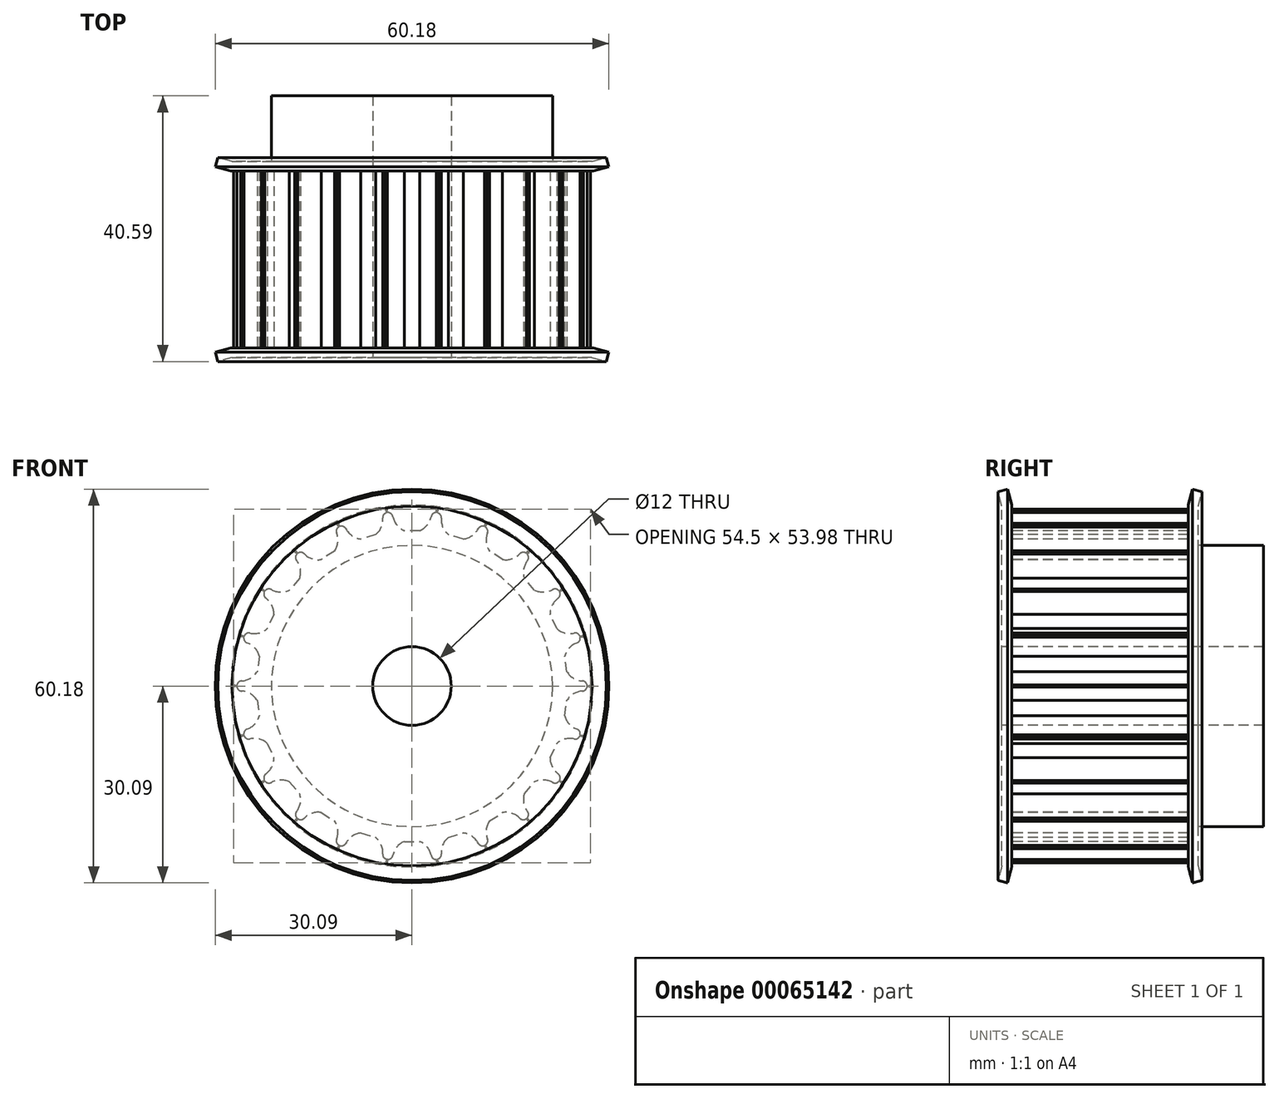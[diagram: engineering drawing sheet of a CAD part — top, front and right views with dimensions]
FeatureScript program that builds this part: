
annotation { "Feature Type Name" : "Feature", "Feature Type Description" : "" }
export const myFeature = defineFeature(function(context is Context, id is Id, definition is map)
    precondition{}
    {
        {
            var Q0;
            Q0=qCreatedBy(makeId("Right.planeOp"),FACE);
            var sketch = newSketch(context, id + "F0", { "sketchPlane" : qUnion([Q0])});
            skLineSegment(sketch, "E0", {"start": v(-21.52, 0) * mm, "end": v(23.89, 0) * mm, "construction": true});
            skLineSegment(sketch, "E1", {"start": v(0, 6) * mm, "end": v(0, 27.25) * mm});
            skLineSegment(sketch, "E2", {"start": v(0, 27.25) * mm, "end": v(30, 27.25) * mm});
            skLineSegment(sketch, "E3", {"start": v(30, 27.25) * mm, "end": v(30, 21.5) * mm});
            skLineSegment(sketch, "E4", {"start": v(30, 21.5) * mm, "end": v(40, 21.5) * mm});
            skLineSegment(sketch, "E5", {"start": v(40, 21.5) * mm, "end": v(40, 6) * mm});
            skLineSegment(sketch, "E6", {"start": v(40, 6) * mm, "end": v(0, 6) * mm});
            skSolve(sketch);
        }
        {
            var Q0;
            Q0 = qSketchRegion(id + "F0", true);
            var Q1;
            Q1=sQuery(id+"F0.wireOp",EDGE,"E0");
            revolve(context, id + "F1", {"entities" : qUnion([Q0]), "axis" : qUnion([Q1]), "revolveType" : RevolveType.FULL});
        }
        {
            var Q0;
            Q0=makeQuery(id+"F1.opRevolve","SWEPT_FACE",FACE,{"disambiguationData":[OSD([sQuery(id+"F0.wireOp",EDGE,"E1")])]});
            var sketch = newSketch(context, id + "F2", { "sketchPlane" : qUnion([Q0])});
            skArc(sketch, "E7", {"start": v(-2.94, 25.9) * mm, "mid": v(-2.33, 24.61) * mm, "end": v(-1.2, 23.75) * mm});
            skLineSegment(sketch, "E8.bottom", {"start": v(-3.75, 28.5) * mm, "end": v(3.75, 28.5) * mm});
            skLineSegment(sketch, "E8.top", {"start": v(-3.75, 26.5) * mm, "end": v(-3.67, 26.5) * mm});
            skLineSegment(sketch, "E8.left", {"start": v(-3.75, 28.5) * mm, "end": v(-3.75, 26.5) * mm});
            skLineSegment(sketch, "E8.right", {"start": v(3.75, 28.5) * mm, "end": v(3.75, 26.5) * mm});
            skArc(sketch, "E9.filletArc", {"start": v(-2.94, 25.9) * mm, "mid": v(-3.2, 26.33) * mm, "end": v(-3.67, 26.5) * mm});
            skLineSegment(sketch, "E10", {"start": v(3.67, 26.5) * mm, "end": v(3.75, 26.5) * mm});
            skPoint(sketch, "E11.visualSharp", {"position": v(3, 26.5) * mm});
            skArc(sketch, "E11.filletArc", {"start": v(3.67, 26.5) * mm, "mid": v(3.2, 26.33) * mm, "end": v(2.94, 25.9) * mm});
            skLineSegment(sketch, "E12", {"start": v(-1.2, 23.75) * mm, "end": v(1.2, 23.75) * mm});
            skArc(sketch, "E13.trimOffspring", {"start": v(1.2, 23.75) * mm, "mid": v(2.33, 24.61) * mm, "end": v(2.94, 25.9) * mm});
            skLineSegment(sketch, "E14.1.0", {"start": v(-11.63, 26.29) * mm, "end": v(-4.43, 28.4) * mm});
            skLineSegment(sketch, "E14.1.1", {"start": v(-11.63, 26.29) * mm, "end": v(-11.06, 24.37) * mm});
            skArc(sketch, "E14.1.2", {"start": v(-10.12, 24.02) * mm, "mid": v(-10.49, 24.36) * mm, "end": v(-11, 24.4) * mm});
            skArc(sketch, "E14.1.3", {"start": v(-10.12, 24.02) * mm, "mid": v(-9.17, 22.96) * mm, "end": v(-7.84, 22.45) * mm});
            skLineSegment(sketch, "E14.1.4", {"start": v(-7.84, 22.45) * mm, "end": v(-5.54, 23.13) * mm});
            skArc(sketch, "E14.1.5", {"start": v(-5.54, 23.13) * mm, "mid": v(-4.7, 24.27) * mm, "end": v(-4.48, 25.68) * mm});
            skPoint(sketch, "E14.1.6", {"position": v(-4.59, 26.27) * mm});
            skLineSegment(sketch, "E14.1.7", {"start": v(-4.43, 28.4) * mm, "end": v(-3.87, 26.48) * mm});
            skArc(sketch, "E14.1.8", {"start": v(-3.94, 26.46) * mm, "mid": v(-4.35, 26.17) * mm, "end": v(-4.48, 25.68) * mm});
            skLineSegment(sketch, "E14.2.0", {"start": v(-18.56, 21.95) * mm, "end": v(-12.25, 26) * mm});
            skLineSegment(sketch, "E14.2.1", {"start": v(-18.56, 21.95) * mm, "end": v(-17.48, 20.27) * mm});
            skArc(sketch, "E14.2.2", {"start": v(-16.48, 20.2) * mm, "mid": v(-16.93, 20.42) * mm, "end": v(-17.42, 20.3) * mm});
            skArc(sketch, "E14.2.3", {"start": v(-16.48, 20.2) * mm, "mid": v(-15.27, 19.44) * mm, "end": v(-13.85, 19.33) * mm});
            skLineSegment(sketch, "E14.2.4", {"start": v(-13.85, 19.33) * mm, "end": v(-11.83, 20.63) * mm});
            skArc(sketch, "E14.2.5", {"start": v(-11.83, 20.63) * mm, "mid": v(-11.34, 21.97) * mm, "end": v(-11.53, 23.38) * mm});
            skPoint(sketch, "E14.2.6", {"position": v(-11.8, 23.92) * mm});
            skLineSegment(sketch, "E14.2.7", {"start": v(-12.25, 26) * mm, "end": v(-11.17, 24.32) * mm});
            skArc(sketch, "E14.2.8", {"start": v(-11.24, 24.28) * mm, "mid": v(-11.54, 23.88) * mm, "end": v(-11.53, 23.38) * mm});
            skLineSegment(sketch, "E14.3.0", {"start": v(-24, 15.83) * mm, "end": v(-19.08, 21.5) * mm});
            skLineSegment(sketch, "E14.3.1", {"start": v(-24, 15.83) * mm, "end": v(-22.48, 14.52) * mm});
            skArc(sketch, "E14.3.2", {"start": v(-21.5, 14.74) * mm, "mid": v(-22, 14.82) * mm, "end": v(-22.43, 14.58) * mm});
            skArc(sketch, "E14.3.3", {"start": v(-21.5, 14.74) * mm, "mid": v(-20.13, 14.36) * mm, "end": v(-18.73, 14.65) * mm});
            skLineSegment(sketch, "E14.3.4", {"start": v(-18.73, 14.65) * mm, "end": v(-17.16, 16.46) * mm});
            skArc(sketch, "E14.3.5", {"start": v(-17.16, 16.46) * mm, "mid": v(-17.07, 17.88) * mm, "end": v(-17.65, 19.18) * mm});
            skPoint(sketch, "E14.3.6", {"position": v(-18.06, 19.62) * mm});
            skLineSegment(sketch, "E14.3.7", {"start": v(-19.08, 21.5) * mm, "end": v(-17.57, 20.19) * mm});
            skArc(sketch, "E14.3.8", {"start": v(-17.62, 20.13) * mm, "mid": v(-17.8, 19.66) * mm, "end": v(-17.65, 19.18) * mm});
            skLineSegment(sketch, "E14.4.0", {"start": v(-27.48, 8.43) * mm, "end": v(-24.37, 15.25) * mm});
            skLineSegment(sketch, "E14.4.1", {"start": v(-27.48, 8.43) * mm, "end": v(-25.66, 7.6) * mm});
            skArc(sketch, "E14.4.2", {"start": v(-24.78, 8.09) * mm, "mid": v(-25.28, 8.03) * mm, "end": v(-25.63, 7.67) * mm});
            skArc(sketch, "E14.4.3", {"start": v(-24.78, 8.09) * mm, "mid": v(-23.36, 8.1) * mm, "end": v(-22.1, 8.78) * mm});
            skLineSegment(sketch, "E14.4.4", {"start": v(-22.1, 8.78) * mm, "end": v(-21.1, 10.96) * mm});
            skArc(sketch, "E14.4.5", {"start": v(-21.1, 10.96) * mm, "mid": v(-21.42, 12.35) * mm, "end": v(-22.34, 13.43) * mm});
            skPoint(sketch, "E14.4.6", {"position": v(-22.86, 13.74) * mm});
            skLineSegment(sketch, "E14.4.7", {"start": v(-24.37, 15.25) * mm, "end": v(-22.55, 14.42) * mm});
            skArc(sketch, "E14.4.8", {"start": v(-22.58, 14.35) * mm, "mid": v(-22.62, 13.85) * mm, "end": v(-22.34, 13.43) * mm});
            skLineSegment(sketch, "E14.5.0", {"start": v(-28.74, 0.34) * mm, "end": v(-27.68, 7.77) * mm});
            skLineSegment(sketch, "E14.5.1", {"start": v(-28.74, 0.34) * mm, "end": v(-26.76, 0.06) * mm});
            skArc(sketch, "E14.5.2", {"start": v(-26.05, 0.78) * mm, "mid": v(-26.52, 0.58) * mm, "end": v(-26.75, 0.13) * mm});
            skArc(sketch, "E14.5.3", {"start": v(-26.05, 0.78) * mm, "mid": v(-24.7, 1.2) * mm, "end": v(-23.68, 2.2) * mm});
            skLineSegment(sketch, "E14.5.4", {"start": v(-23.68, 2.2) * mm, "end": v(-23.34, 4.57) * mm});
            skArc(sketch, "E14.5.5", {"start": v(-23.34, 4.57) * mm, "mid": v(-24.03, 5.81) * mm, "end": v(-25.22, 6.6) * mm});
            skPoint(sketch, "E14.5.6", {"position": v(-25.8, 6.74) * mm});
            skLineSegment(sketch, "E14.5.7", {"start": v(-27.68, 7.77) * mm, "end": v(-25.7, 7.48) * mm});
            skArc(sketch, "E14.5.8", {"start": v(-25.7, 7.4) * mm, "mid": v(-25.6, 6.91) * mm, "end": v(-25.22, 6.6) * mm});
            skLineSegment(sketch, "E14.6.0", {"start": v(-27.68, -7.77) * mm, "end": v(-28.74, -0.34) * mm});
            skLineSegment(sketch, "E14.6.1", {"start": v(-27.68, -7.77) * mm, "end": v(-25.7, -7.48) * mm});
            skArc(sketch, "E14.6.2", {"start": v(-25.22, -6.6) * mm, "mid": v(-25.6, -6.91) * mm, "end": v(-25.7, -7.4) * mm});
            skArc(sketch, "E14.6.3", {"start": v(-25.22, -6.6) * mm, "mid": v(-24.03, -5.81) * mm, "end": v(-23.34, -4.57) * mm});
            skLineSegment(sketch, "E14.6.4", {"start": v(-23.34, -4.57) * mm, "end": v(-23.68, -2.2) * mm});
            skArc(sketch, "E14.6.5", {"start": v(-23.68, -2.2) * mm, "mid": v(-24.7, -1.2) * mm, "end": v(-26.05, -0.78) * mm});
            skPoint(sketch, "E14.6.6", {"position": v(-26.66, -0.8) * mm});
            skLineSegment(sketch, "E14.6.7", {"start": v(-28.74, -0.34) * mm, "end": v(-26.76, -0.06) * mm});
            skArc(sketch, "E14.6.8", {"start": v(-26.75, -0.13) * mm, "mid": v(-26.52, -0.58) * mm, "end": v(-26.05, -0.78) * mm});
            skLineSegment(sketch, "E14.7.0", {"start": v(-24.37, -15.25) * mm, "end": v(-27.48, -8.43) * mm});
            skLineSegment(sketch, "E14.7.1", {"start": v(-24.37, -15.25) * mm, "end": v(-22.55, -14.42) * mm});
            skArc(sketch, "E14.7.2", {"start": v(-22.34, -13.43) * mm, "mid": v(-22.62, -13.85) * mm, "end": v(-22.58, -14.35) * mm});
            skArc(sketch, "E14.7.3", {"start": v(-22.34, -13.43) * mm, "mid": v(-21.42, -12.35) * mm, "end": v(-21.1, -10.96) * mm});
            skLineSegment(sketch, "E14.7.4", {"start": v(-21.1, -10.96) * mm, "end": v(-22.1, -8.78) * mm});
            skArc(sketch, "E14.7.5", {"start": v(-22.1, -8.78) * mm, "mid": v(-23.36, -8.1) * mm, "end": v(-24.78, -8.09) * mm});
            skPoint(sketch, "E14.7.6", {"position": v(-25.35, -8.28) * mm});
            skLineSegment(sketch, "E14.7.7", {"start": v(-27.48, -8.43) * mm, "end": v(-25.66, -7.6) * mm});
            skArc(sketch, "E14.7.8", {"start": v(-25.63, -7.67) * mm, "mid": v(-25.28, -8.03) * mm, "end": v(-24.78, -8.09) * mm});
            skLineSegment(sketch, "E14.8.0", {"start": v(-19.08, -21.5) * mm, "end": v(-24, -15.83) * mm});
            skLineSegment(sketch, "E14.8.1", {"start": v(-19.08, -21.5) * mm, "end": v(-17.57, -20.19) * mm});
            skArc(sketch, "E14.8.2", {"start": v(-17.65, -19.18) * mm, "mid": v(-17.8, -19.66) * mm, "end": v(-17.62, -20.13) * mm});
            skArc(sketch, "E14.8.3", {"start": v(-17.65, -19.18) * mm, "mid": v(-17.07, -17.88) * mm, "end": v(-17.16, -16.46) * mm});
            skLineSegment(sketch, "E14.8.4", {"start": v(-17.16, -16.46) * mm, "end": v(-18.73, -14.65) * mm});
            skArc(sketch, "E14.8.5", {"start": v(-18.73, -14.65) * mm, "mid": v(-20.13, -14.36) * mm, "end": v(-21.5, -14.74) * mm});
            skPoint(sketch, "E14.8.6", {"position": v(-22, -15.09) * mm});
            skLineSegment(sketch, "E14.8.7", {"start": v(-24, -15.83) * mm, "end": v(-22.48, -14.52) * mm});
            skArc(sketch, "E14.8.8", {"start": v(-22.43, -14.58) * mm, "mid": v(-22, -14.82) * mm, "end": v(-21.5, -14.74) * mm});
            skLineSegment(sketch, "E14.9.0", {"start": v(-12.25, -26) * mm, "end": v(-18.56, -21.95) * mm});
            skLineSegment(sketch, "E14.9.1", {"start": v(-12.25, -26) * mm, "end": v(-11.17, -24.32) * mm});
            skArc(sketch, "E14.9.2", {"start": v(-11.53, -23.38) * mm, "mid": v(-11.54, -23.88) * mm, "end": v(-11.24, -24.28) * mm});
            skArc(sketch, "E14.9.3", {"start": v(-11.53, -23.38) * mm, "mid": v(-11.34, -21.97) * mm, "end": v(-11.83, -20.63) * mm});
            skLineSegment(sketch, "E14.9.4", {"start": v(-11.83, -20.63) * mm, "end": v(-13.85, -19.33) * mm});
            skArc(sketch, "E14.9.5", {"start": v(-13.85, -19.33) * mm, "mid": v(-15.27, -19.44) * mm, "end": v(-16.48, -20.2) * mm});
            skPoint(sketch, "E14.9.6", {"position": v(-16.85, -20.67) * mm});
            skLineSegment(sketch, "E14.9.7", {"start": v(-18.56, -21.95) * mm, "end": v(-17.48, -20.27) * mm});
            skArc(sketch, "E14.9.8", {"start": v(-17.42, -20.3) * mm, "mid": v(-16.93, -20.42) * mm, "end": v(-16.48, -20.2) * mm});
            skLineSegment(sketch, "E14.10.0", {"start": v(-4.43, -28.4) * mm, "end": v(-11.63, -26.29) * mm});
            skLineSegment(sketch, "E14.10.1", {"start": v(-4.43, -28.4) * mm, "end": v(-3.87, -26.48) * mm});
            skArc(sketch, "E14.10.2", {"start": v(-4.48, -25.68) * mm, "mid": v(-4.35, -26.17) * mm, "end": v(-3.94, -26.46) * mm});
            skArc(sketch, "E14.10.3", {"start": v(-4.48, -25.68) * mm, "mid": v(-4.7, -24.27) * mm, "end": v(-5.54, -23.13) * mm});
            skLineSegment(sketch, "E14.10.4", {"start": v(-5.54, -23.13) * mm, "end": v(-7.84, -22.45) * mm});
            skArc(sketch, "E14.10.5", {"start": v(-7.84, -22.45) * mm, "mid": v(-9.17, -22.96) * mm, "end": v(-10.12, -24.02) * mm});
            skPoint(sketch, "E14.10.6", {"position": v(-10.34, -24.58) * mm});
            skLineSegment(sketch, "E14.10.7", {"start": v(-11.63, -26.29) * mm, "end": v(-11.06, -24.37) * mm});
            skArc(sketch, "E14.10.8", {"start": v(-11, -24.4) * mm, "mid": v(-10.49, -24.36) * mm, "end": v(-10.12, -24.02) * mm});
            skLineSegment(sketch, "E14.11.0", {"start": v(3.75, -28.5) * mm, "end": v(-3.75, -28.5) * mm});
            skLineSegment(sketch, "E14.11.1", {"start": v(3.75, -28.5) * mm, "end": v(3.75, -26.5) * mm});
            skArc(sketch, "E14.11.2", {"start": v(2.94, -25.9) * mm, "mid": v(3.2, -26.33) * mm, "end": v(3.67, -26.5) * mm});
            skArc(sketch, "E14.11.3", {"start": v(2.94, -25.9) * mm, "mid": v(2.33, -24.61) * mm, "end": v(1.2, -23.75) * mm});
            skLineSegment(sketch, "E14.11.4", {"start": v(1.2, -23.75) * mm, "end": v(-1.2, -23.75) * mm});
            skArc(sketch, "E14.11.5", {"start": v(-1.2, -23.75) * mm, "mid": v(-2.33, -24.61) * mm, "end": v(-2.94, -25.9) * mm});
            skPoint(sketch, "E14.11.6", {"position": v(-3, -26.5) * mm});
            skLineSegment(sketch, "E14.11.7", {"start": v(-3.75, -28.5) * mm, "end": v(-3.75, -26.5) * mm});
            skArc(sketch, "E14.11.8", {"start": v(-3.67, -26.5) * mm, "mid": v(-3.2, -26.33) * mm, "end": v(-2.94, -25.9) * mm});
            skLineSegment(sketch, "E14.12.0", {"start": v(11.63, -26.29) * mm, "end": v(4.43, -28.4) * mm});
            skLineSegment(sketch, "E14.12.1", {"start": v(11.63, -26.29) * mm, "end": v(11.06, -24.37) * mm});
            skArc(sketch, "E14.12.2", {"start": v(10.12, -24.02) * mm, "mid": v(10.49, -24.36) * mm, "end": v(11, -24.4) * mm});
            skArc(sketch, "E14.12.3", {"start": v(10.12, -24.02) * mm, "mid": v(9.17, -22.96) * mm, "end": v(7.84, -22.45) * mm});
            skLineSegment(sketch, "E14.12.4", {"start": v(7.84, -22.45) * mm, "end": v(5.54, -23.13) * mm});
            skArc(sketch, "E14.12.5", {"start": v(5.54, -23.13) * mm, "mid": v(4.7, -24.27) * mm, "end": v(4.48, -25.68) * mm});
            skPoint(sketch, "E14.12.6", {"position": v(4.59, -26.27) * mm});
            skLineSegment(sketch, "E14.12.7", {"start": v(4.43, -28.4) * mm, "end": v(3.87, -26.48) * mm});
            skArc(sketch, "E14.12.8", {"start": v(3.94, -26.46) * mm, "mid": v(4.35, -26.17) * mm, "end": v(4.48, -25.68) * mm});
            skLineSegment(sketch, "E14.13.0", {"start": v(18.56, -21.95) * mm, "end": v(12.25, -26) * mm});
            skLineSegment(sketch, "E14.13.1", {"start": v(18.56, -21.95) * mm, "end": v(17.48, -20.27) * mm});
            skArc(sketch, "E14.13.2", {"start": v(16.48, -20.2) * mm, "mid": v(16.93, -20.42) * mm, "end": v(17.42, -20.3) * mm});
            skArc(sketch, "E14.13.3", {"start": v(16.48, -20.2) * mm, "mid": v(15.27, -19.44) * mm, "end": v(13.85, -19.33) * mm});
            skLineSegment(sketch, "E14.13.4", {"start": v(13.85, -19.33) * mm, "end": v(11.83, -20.63) * mm});
            skArc(sketch, "E14.13.5", {"start": v(11.83, -20.63) * mm, "mid": v(11.34, -21.97) * mm, "end": v(11.53, -23.38) * mm});
            skPoint(sketch, "E14.13.6", {"position": v(11.8, -23.92) * mm});
            skLineSegment(sketch, "E14.13.7", {"start": v(12.25, -26) * mm, "end": v(11.17, -24.32) * mm});
            skArc(sketch, "E14.13.8", {"start": v(11.24, -24.28) * mm, "mid": v(11.54, -23.88) * mm, "end": v(11.53, -23.38) * mm});
            skLineSegment(sketch, "E14.14.0", {"start": v(24, -15.83) * mm, "end": v(19.08, -21.5) * mm});
            skLineSegment(sketch, "E14.14.1", {"start": v(24, -15.83) * mm, "end": v(22.48, -14.52) * mm});
            skArc(sketch, "E14.14.2", {"start": v(21.5, -14.74) * mm, "mid": v(22, -14.82) * mm, "end": v(22.43, -14.58) * mm});
            skArc(sketch, "E14.14.3", {"start": v(21.5, -14.74) * mm, "mid": v(20.13, -14.36) * mm, "end": v(18.73, -14.65) * mm});
            skLineSegment(sketch, "E14.14.4", {"start": v(18.73, -14.65) * mm, "end": v(17.16, -16.46) * mm});
            skArc(sketch, "E14.14.5", {"start": v(17.16, -16.46) * mm, "mid": v(17.07, -17.88) * mm, "end": v(17.65, -19.18) * mm});
            skPoint(sketch, "E14.14.6", {"position": v(18.06, -19.62) * mm});
            skLineSegment(sketch, "E14.14.7", {"start": v(19.08, -21.5) * mm, "end": v(17.57, -20.19) * mm});
            skArc(sketch, "E14.14.8", {"start": v(17.62, -20.13) * mm, "mid": v(17.8, -19.66) * mm, "end": v(17.65, -19.18) * mm});
            skLineSegment(sketch, "E14.15.0", {"start": v(27.48, -8.43) * mm, "end": v(24.37, -15.25) * mm});
            skLineSegment(sketch, "E14.15.1", {"start": v(27.48, -8.43) * mm, "end": v(25.66, -7.6) * mm});
            skArc(sketch, "E14.15.2", {"start": v(24.78, -8.09) * mm, "mid": v(25.28, -8.03) * mm, "end": v(25.63, -7.67) * mm});
            skArc(sketch, "E14.15.3", {"start": v(24.78, -8.09) * mm, "mid": v(23.36, -8.1) * mm, "end": v(22.1, -8.78) * mm});
            skLineSegment(sketch, "E14.15.4", {"start": v(22.1, -8.78) * mm, "end": v(21.1, -10.96) * mm});
            skArc(sketch, "E14.15.5", {"start": v(21.1, -10.96) * mm, "mid": v(21.42, -12.35) * mm, "end": v(22.34, -13.43) * mm});
            skPoint(sketch, "E14.15.6", {"position": v(22.86, -13.74) * mm});
            skLineSegment(sketch, "E14.15.7", {"start": v(24.37, -15.25) * mm, "end": v(22.55, -14.42) * mm});
            skArc(sketch, "E14.15.8", {"start": v(22.58, -14.35) * mm, "mid": v(22.62, -13.85) * mm, "end": v(22.34, -13.43) * mm});
            skLineSegment(sketch, "E14.16.0", {"start": v(28.74, -0.34) * mm, "end": v(27.68, -7.77) * mm});
            skLineSegment(sketch, "E14.16.1", {"start": v(28.74, -0.34) * mm, "end": v(26.76, -0.06) * mm});
            skArc(sketch, "E14.16.2", {"start": v(26.05, -0.78) * mm, "mid": v(26.52, -0.58) * mm, "end": v(26.75, -0.13) * mm});
            skArc(sketch, "E14.16.3", {"start": v(26.05, -0.78) * mm, "mid": v(24.7, -1.2) * mm, "end": v(23.68, -2.2) * mm});
            skLineSegment(sketch, "E14.16.4", {"start": v(23.68, -2.2) * mm, "end": v(23.34, -4.57) * mm});
            skArc(sketch, "E14.16.5", {"start": v(23.34, -4.57) * mm, "mid": v(24.03, -5.81) * mm, "end": v(25.22, -6.6) * mm});
            skPoint(sketch, "E14.16.6", {"position": v(25.8, -6.74) * mm});
            skLineSegment(sketch, "E14.16.7", {"start": v(27.68, -7.77) * mm, "end": v(25.7, -7.48) * mm});
            skArc(sketch, "E14.16.8", {"start": v(25.7, -7.4) * mm, "mid": v(25.6, -6.91) * mm, "end": v(25.22, -6.6) * mm});
            skLineSegment(sketch, "E14.17.0", {"start": v(27.68, 7.77) * mm, "end": v(28.74, 0.34) * mm});
            skLineSegment(sketch, "E14.17.1", {"start": v(27.68, 7.77) * mm, "end": v(25.7, 7.48) * mm});
            skArc(sketch, "E14.17.2", {"start": v(25.22, 6.6) * mm, "mid": v(25.6, 6.91) * mm, "end": v(25.7, 7.4) * mm});
            skArc(sketch, "E14.17.3", {"start": v(25.22, 6.6) * mm, "mid": v(24.03, 5.81) * mm, "end": v(23.34, 4.57) * mm});
            skLineSegment(sketch, "E14.17.4", {"start": v(23.34, 4.57) * mm, "end": v(23.68, 2.2) * mm});
            skArc(sketch, "E14.17.5", {"start": v(23.68, 2.2) * mm, "mid": v(24.7, 1.2) * mm, "end": v(26.05, 0.78) * mm});
            skPoint(sketch, "E14.17.6", {"position": v(26.66, 0.8) * mm});
            skLineSegment(sketch, "E14.17.7", {"start": v(28.74, 0.34) * mm, "end": v(26.76, 0.06) * mm});
            skArc(sketch, "E14.17.8", {"start": v(26.75, 0.13) * mm, "mid": v(26.52, 0.58) * mm, "end": v(26.05, 0.78) * mm});
            skLineSegment(sketch, "E14.18.0", {"start": v(24.37, 15.25) * mm, "end": v(27.48, 8.43) * mm});
            skLineSegment(sketch, "E14.18.1", {"start": v(24.37, 15.25) * mm, "end": v(22.55, 14.42) * mm});
            skArc(sketch, "E14.18.2", {"start": v(22.34, 13.43) * mm, "mid": v(22.62, 13.85) * mm, "end": v(22.58, 14.35) * mm});
            skArc(sketch, "E14.18.3", {"start": v(22.34, 13.43) * mm, "mid": v(21.42, 12.35) * mm, "end": v(21.1, 10.96) * mm});
            skLineSegment(sketch, "E14.18.4", {"start": v(21.1, 10.96) * mm, "end": v(22.1, 8.78) * mm});
            skArc(sketch, "E14.18.5", {"start": v(22.1, 8.78) * mm, "mid": v(23.36, 8.1) * mm, "end": v(24.78, 8.09) * mm});
            skPoint(sketch, "E14.18.6", {"position": v(25.35, 8.28) * mm});
            skLineSegment(sketch, "E14.18.7", {"start": v(27.48, 8.43) * mm, "end": v(25.66, 7.6) * mm});
            skArc(sketch, "E14.18.8", {"start": v(25.63, 7.67) * mm, "mid": v(25.28, 8.03) * mm, "end": v(24.78, 8.09) * mm});
            skLineSegment(sketch, "E14.19.0", {"start": v(19.08, 21.5) * mm, "end": v(24, 15.83) * mm});
            skLineSegment(sketch, "E14.19.1", {"start": v(19.08, 21.5) * mm, "end": v(17.57, 20.19) * mm});
            skArc(sketch, "E14.19.2", {"start": v(17.65, 19.18) * mm, "mid": v(17.8, 19.66) * mm, "end": v(17.62, 20.13) * mm});
            skArc(sketch, "E14.19.3", {"start": v(17.65, 19.18) * mm, "mid": v(17.07, 17.88) * mm, "end": v(17.16, 16.46) * mm});
            skLineSegment(sketch, "E14.19.4", {"start": v(17.16, 16.46) * mm, "end": v(18.73, 14.65) * mm});
            skArc(sketch, "E14.19.5", {"start": v(18.73, 14.65) * mm, "mid": v(20.13, 14.36) * mm, "end": v(21.5, 14.74) * mm});
            skPoint(sketch, "E14.19.6", {"position": v(22, 15.09) * mm});
            skLineSegment(sketch, "E14.19.7", {"start": v(24, 15.83) * mm, "end": v(22.48, 14.52) * mm});
            skArc(sketch, "E14.19.8", {"start": v(22.43, 14.58) * mm, "mid": v(22, 14.82) * mm, "end": v(21.5, 14.74) * mm});
            skLineSegment(sketch, "E14.20.0", {"start": v(12.25, 26) * mm, "end": v(18.56, 21.95) * mm});
            skLineSegment(sketch, "E14.20.1", {"start": v(12.25, 26) * mm, "end": v(11.17, 24.32) * mm});
            skArc(sketch, "E14.20.2", {"start": v(11.53, 23.38) * mm, "mid": v(11.54, 23.88) * mm, "end": v(11.24, 24.28) * mm});
            skArc(sketch, "E14.20.3", {"start": v(11.53, 23.38) * mm, "mid": v(11.34, 21.97) * mm, "end": v(11.83, 20.63) * mm});
            skLineSegment(sketch, "E14.20.4", {"start": v(11.83, 20.63) * mm, "end": v(13.85, 19.33) * mm});
            skArc(sketch, "E14.20.5", {"start": v(13.85, 19.33) * mm, "mid": v(15.27, 19.44) * mm, "end": v(16.48, 20.2) * mm});
            skPoint(sketch, "E14.20.6", {"position": v(16.85, 20.67) * mm});
            skLineSegment(sketch, "E14.20.7", {"start": v(18.56, 21.95) * mm, "end": v(17.48, 20.27) * mm});
            skArc(sketch, "E14.20.8", {"start": v(17.42, 20.3) * mm, "mid": v(16.93, 20.42) * mm, "end": v(16.48, 20.2) * mm});
            skLineSegment(sketch, "E14.21.0", {"start": v(4.43, 28.4) * mm, "end": v(11.63, 26.29) * mm});
            skLineSegment(sketch, "E14.21.1", {"start": v(4.43, 28.4) * mm, "end": v(3.87, 26.48) * mm});
            skArc(sketch, "E14.21.2", {"start": v(4.48, 25.68) * mm, "mid": v(4.35, 26.17) * mm, "end": v(3.94, 26.46) * mm});
            skArc(sketch, "E14.21.3", {"start": v(4.48, 25.68) * mm, "mid": v(4.7, 24.27) * mm, "end": v(5.54, 23.13) * mm});
            skLineSegment(sketch, "E14.21.4", {"start": v(5.54, 23.13) * mm, "end": v(7.84, 22.45) * mm});
            skArc(sketch, "E14.21.5", {"start": v(7.84, 22.45) * mm, "mid": v(9.17, 22.96) * mm, "end": v(10.12, 24.02) * mm});
            skPoint(sketch, "E14.21.6", {"position": v(10.34, 24.58) * mm});
            skLineSegment(sketch, "E14.21.7", {"start": v(11.63, 26.29) * mm, "end": v(11.06, 24.37) * mm});
            skArc(sketch, "E14.21.8", {"start": v(11, 24.4) * mm, "mid": v(10.49, 24.36) * mm, "end": v(10.12, 24.02) * mm});
            skPoint(sketch, "E14.center", {"position": v(0, 0) * mm});
            skLineSegment(sketch, "E15", {"start": v(-11.06, 24.37) * mm, "end": v(-11, 24.4) * mm});
            skLineSegment(sketch, "E16", {"start": v(-11.24, 24.28) * mm, "end": v(-11.17, 24.32) * mm});
            skLineSegment(sketch, "E17", {"start": v(-17.48, 20.27) * mm, "end": v(-17.42, 20.3) * mm});
            skLineSegment(sketch, "E18", {"start": v(-17.62, 20.13) * mm, "end": v(-17.57, 20.19) * mm});
            skLineSegment(sketch, "E19", {"start": v(-3.94, 26.46) * mm, "end": v(-3.87, 26.48) * mm});
            skLineSegment(sketch, "E20", {"start": v(3.87, 26.48) * mm, "end": v(3.94, 26.46) * mm});
            skLineSegment(sketch, "E21", {"start": v(11, 24.4) * mm, "end": v(11.06, 24.37) * mm});
            skLineSegment(sketch, "E22", {"start": v(11.17, 24.32) * mm, "end": v(11.24, 24.28) * mm});
            skLineSegment(sketch, "E23", {"start": v(17.42, 20.3) * mm, "end": v(17.48, 20.27) * mm});
            skLineSegment(sketch, "E24", {"start": v(17.57, 20.19) * mm, "end": v(17.62, 20.13) * mm});
            skLineSegment(sketch, "E25", {"start": v(22.43, 14.58) * mm, "end": v(22.48, 14.52) * mm});
            skLineSegment(sketch, "E26", {"start": v(22.55, 14.42) * mm, "end": v(22.58, 14.35) * mm});
            skLineSegment(sketch, "E27", {"start": v(25.63, 7.67) * mm, "end": v(25.66, 7.6) * mm});
            skLineSegment(sketch, "E28", {"start": v(25.7, 7.48) * mm, "end": v(25.7, 7.4) * mm});
            skLineSegment(sketch, "E29", {"start": v(26.75, 0.13) * mm, "end": v(26.76, 0.06) * mm});
            skLineSegment(sketch, "E30", {"start": v(26.76, -0.06) * mm, "end": v(26.75, -0.13) * mm});
            skLineSegment(sketch, "E31", {"start": v(25.7, -7.4) * mm, "end": v(25.7, -7.48) * mm});
            skLineSegment(sketch, "E32", {"start": v(25.66, -7.6) * mm, "end": v(25.63, -7.67) * mm});
            skLineSegment(sketch, "E33", {"start": v(22.58, -14.35) * mm, "end": v(22.55, -14.42) * mm});
            skLineSegment(sketch, "E34", {"start": v(22.48, -14.52) * mm, "end": v(22.43, -14.58) * mm});
            skLineSegment(sketch, "E35", {"start": v(17.42, -20.3) * mm, "end": v(17.48, -20.27) * mm});
            skLineSegment(sketch, "E36", {"start": v(17.57, -20.19) * mm, "end": v(17.62, -20.13) * mm});
            skLineSegment(sketch, "E37", {"start": v(11, -24.4) * mm, "end": v(11.06, -24.37) * mm});
            skLineSegment(sketch, "E38", {"start": v(11.17, -24.32) * mm, "end": v(11.24, -24.28) * mm});
            skLineSegment(sketch, "E39", {"start": v(3.67, -26.5) * mm, "end": v(3.75, -26.5) * mm});
            skLineSegment(sketch, "E40", {"start": v(3.87, -26.48) * mm, "end": v(3.94, -26.46) * mm});
            skLineSegment(sketch, "E41", {"start": v(-3.94, -26.46) * mm, "end": v(-3.87, -26.48) * mm});
            skLineSegment(sketch, "E42", {"start": v(-3.75, -26.5) * mm, "end": v(-3.67, -26.5) * mm});
            skLineSegment(sketch, "E43", {"start": v(-11.24, -24.28) * mm, "end": v(-11.17, -24.32) * mm});
            skLineSegment(sketch, "E44", {"start": v(-11.06, -24.37) * mm, "end": v(-11, -24.4) * mm});
            skLineSegment(sketch, "E45", {"start": v(-17.62, -20.13) * mm, "end": v(-17.57, -20.19) * mm});
            skLineSegment(sketch, "E46", {"start": v(-17.48, -20.27) * mm, "end": v(-17.42, -20.3) * mm});
            skLineSegment(sketch, "E47", {"start": v(-22.58, -14.35) * mm, "end": v(-22.55, -14.42) * mm});
            skLineSegment(sketch, "E48", {"start": v(-22.48, -14.52) * mm, "end": v(-22.43, -14.58) * mm});
            skLineSegment(sketch, "E49", {"start": v(-25.7, -7.4) * mm, "end": v(-25.7, -7.48) * mm});
            skLineSegment(sketch, "E50", {"start": v(-25.66, -7.6) * mm, "end": v(-25.63, -7.67) * mm});
            skLineSegment(sketch, "E51", {"start": v(-26.76, -0.06) * mm, "end": v(-26.75, -0.13) * mm});
            skLineSegment(sketch, "E52", {"start": v(-26.75, 0.13) * mm, "end": v(-26.76, 0.06) * mm});
            skLineSegment(sketch, "E53", {"start": v(-25.63, 7.67) * mm, "end": v(-25.66, 7.6) * mm});
            skLineSegment(sketch, "E54", {"start": v(-25.7, 7.48) * mm, "end": v(-25.7, 7.4) * mm});
            skLineSegment(sketch, "E55", {"start": v(-22.43, 14.58) * mm, "end": v(-22.48, 14.52) * mm});
            skLineSegment(sketch, "E56", {"start": v(-22.55, 14.42) * mm, "end": v(-22.58, 14.35) * mm});
            skSolve(sketch);
        }
        {
            var Q0;
            Q0 = qSketchRegion(id + "F2", true);
            extrude(context, id + "F3", {"entities" : qUnion([Q0]), "operationType" : NewBodyOperationType.REMOVE, "endBound" : BoundingType.THROUGH_ALL, "oppositeDirection" : true, "depth" : 25.4 * mm});
        }
        {
            var Q0;
            Q0=qCreatedBy(makeId("Right.planeOp"),FACE);
            var sketch = newSketch(context, id + "F4", { "sketchPlane" : qUnion([Q0])});
            skLineSegment(sketch, "E57.bottom", {"start": v(0, 22.7) * mm, "end": v(1.5, 22.7) * mm});
            skLineSegment(sketch, "E57.top", {"start": v(0, 27.7) * mm, "end": v(1.5, 27.7) * mm});
            skLineSegment(sketch, "E57.left", {"start": v(0, 22.7) * mm, "end": v(0, 27.7) * mm});
            skLineSegment(sketch, "E57.right", {"start": v(1.5, 22.7) * mm, "end": v(1.5, 27.7) * mm});
            skLineSegment(sketch, "E58", {"start": v(15, 41.03) * mm, "end": v(15, -28.92) * mm, "construction": true});
            skLineSegment(sketch, "E59.MirrorCS", {"start": v(28.5, 22.7) * mm, "end": v(28.5, 27.7) * mm});
            skLineSegment(sketch, "E60.MirrorCS", {"start": v(30, 22.7) * mm, "end": v(28.5, 22.7) * mm});
            skLineSegment(sketch, "E61.MirrorCS", {"start": v(30, 22.7) * mm, "end": v(30, 27.7) * mm});
            skLineSegment(sketch, "E62.MirrorCS", {"start": v(30, 27.7) * mm, "end": v(28.5, 27.7) * mm});
            skLineSegment(sketch, "E63", {"start": v(1.5, 27.7) * mm, "end": v(0.86, 30.1) * mm});
            skLineSegment(sketch, "E64", {"start": v(0.86, 30.1) * mm, "end": v(-0.6, 29.7) * mm});
            skLineSegment(sketch, "E65", {"start": v(-0.6, 29.7) * mm, "end": v(0.05, 27.3) * mm});
            skLineSegment(sketch, "E66", {"start": v(0.05, 27.3) * mm, "end": v(1.5, 27.7) * mm});
            skLineSegment(sketch, "E67.MirrorCS", {"start": v(29.14, 30.1) * mm, "end": v(30.6, 29.7) * mm});
            skLineSegment(sketch, "E68.MirrorCS", {"start": v(30.6, 29.7) * mm, "end": v(29.95, 27.3) * mm});
            skLineSegment(sketch, "E69.MirrorCS", {"start": v(28.5, 27.7) * mm, "end": v(29.14, 30.1) * mm});
            skLineSegment(sketch, "E70.MirrorCS", {"start": v(29.95, 27.3) * mm, "end": v(28.5, 27.7) * mm});
            skSolve(sketch);
        }
        {
            var Q0;
            Q0=qCreatedBy(makeId("Right.planeOp"),FACE);
            var sketch = newSketch(context, id + "F5", { "sketchPlane" : qUnion([Q0])});
            skLineSegment(sketch, "E71", {"start": v(-38.96, 0) * mm, "end": v(60.95, 0) * mm, "construction": true});
            skSolve(sketch);
        }
        {
            var Q0;
            Q0 = qSketchRegion(id + "F4", true);
            var Q1;
            Q1=sQuery(id+"F5.wireOp",EDGE,"E71");
            revolve(context, id + "F6", {"operationType" : NewBodyOperationType.ADD, "entities" : qUnion([Q0]), "axis" : qUnion([Q1]), "revolveType" : RevolveType.FULL});
        }
    });
